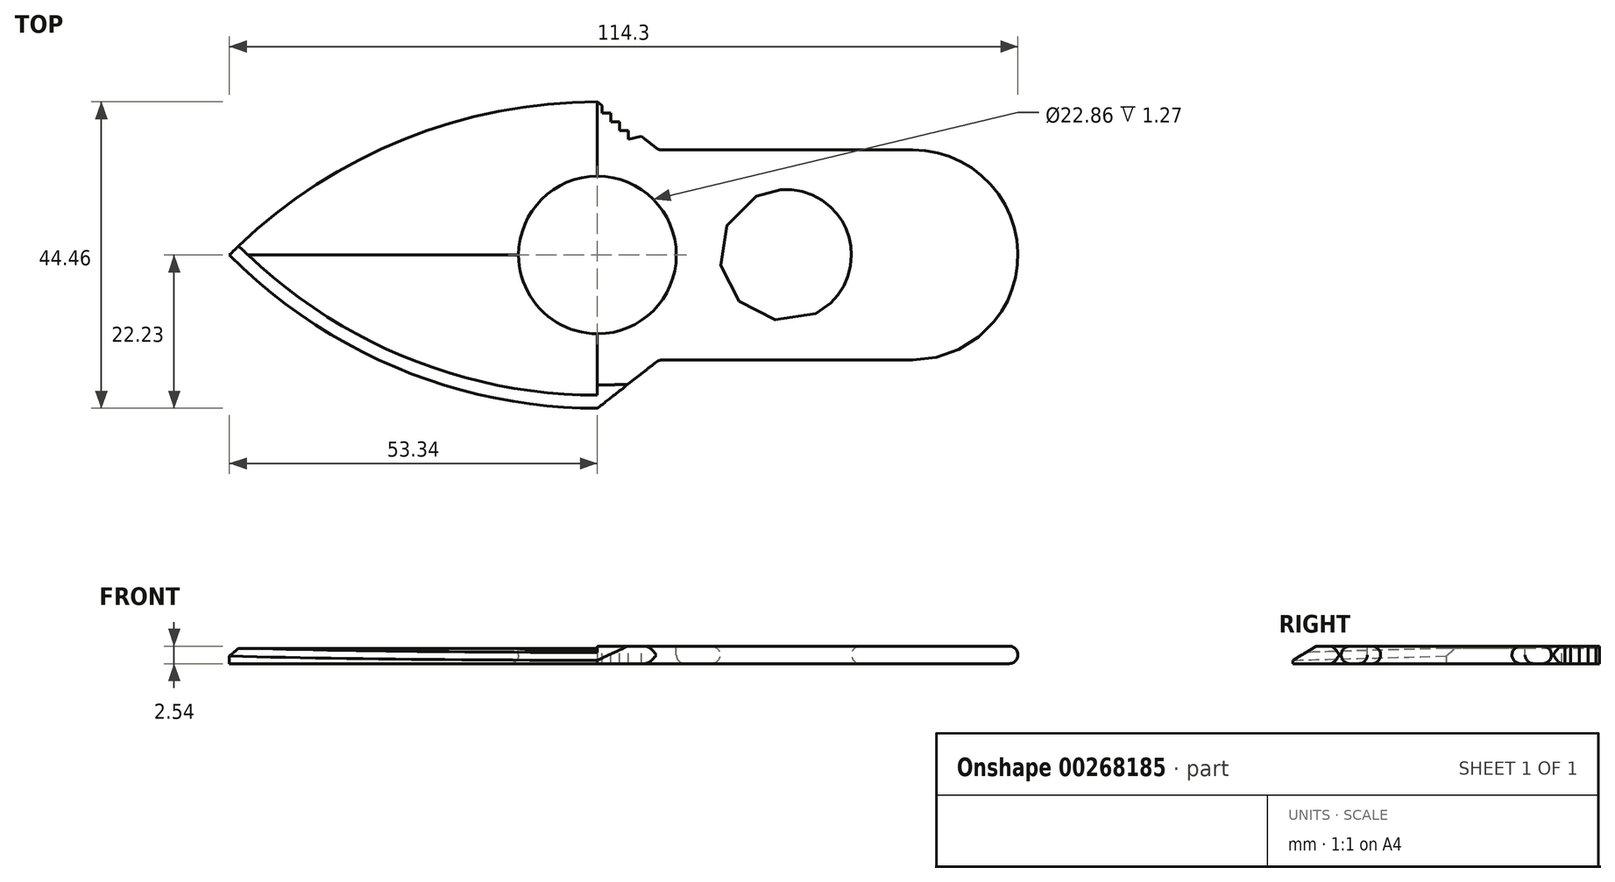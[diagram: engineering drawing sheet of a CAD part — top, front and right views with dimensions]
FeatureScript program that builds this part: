
annotation { "Feature Type Name" : "Feature", "Feature Type Description" : "" }
export const myFeature = defineFeature(function(context is Context, id is Id, definition is map)
    precondition{}
    {
        {
            var Q0;
            Q0=qCreatedBy(makeId("Top.planeOp"),FACE);
            var sketch = newSketch(context, id + "F0", { "sketchPlane" : qUnion([Q0])});
            skLineSegment(sketch, "E0", {"start": v(-57.15, 0) * mm, "end": v(57.15, 0) * mm});
            skArc(sketch, "E1", {"start": v(-3.81, 22.23) * mm, "mid": v(-32.7, 16.45) * mm, "end": v(-57.15, 0) * mm});
            skLineSegment(sketch, "E2", {"start": v(-3.8, 22.23) * mm, "end": v(-3.8, 0) * mm, "construction": true});
            skLineSegment(sketch, "E3", {"start": v(5.08, 15.24) * mm, "end": v(41.91, 15.24) * mm});
            skLineSegment(sketch, "E4", {"start": v(41.91, 15.24) * mm, "end": v(41.91, 0) * mm, "construction": true});
            skLineSegment(sketch, "E5", {"start": v(5.08, 15.24) * mm, "end": v(5.08, 0) * mm, "construction": true});
            skLineSegment(sketch, "E6", {"start": v(-3.81, 22.23) * mm, "end": v(5.08, 15.24) * mm});
            skLineSegment(sketch, "E7", {"start": v(-3.81, 22.23) * mm, "end": v(-57.15, 22.22) * mm, "construction": true});
            skArc(sketch, "E8", {"start": v(57.15, 0) * mm, "mid": v(52.69, 10.78) * mm, "end": v(41.91, 15.24) * mm});
            skLineSegment(sketch, "E9", {"start": v(57.15, 0) * mm, "end": v(57.15, 15.24) * mm, "construction": true});
            skSolve(sketch);
        }
        {
            var Q0;
            Q0 = qSketchRegion(id + "F0", true);
            extrude(context, id + "F1", {"entities" : qUnion([Q0]), "endBound" : BoundingType.SYMMETRIC, "depth" : 2.54 * mm});
        }
        {
            var Q0;
            Q0=makeQuery(id+"F1.opExtrude","SWEPT_BODY",BODY,{"disambiguationData":[OSD([sQuery(id+"F0.wireOp",EDGE,"E0"),sQuery(id+"F0.wireOp",EDGE,"E1"),sQuery(id+"F0.wireOp",EDGE,"E3"),sQuery(id+"F0.wireOp",EDGE,"E6"),sQuery(id+"F0.wireOp",EDGE,"E8")])]});
            var Q1;
            Q1=qCreatedBy(makeId("Front.planeOp"),FACE);
            mirror(context, id + "F2", {"operationType" : NewBodyOperationType.ADD, "entities" : qUnion([Q0]), "mirrorPlane" : qUnion([Q1])});
        }
        {
            var Q0;
            {var subQ0=makeQuery(id+"F1.opExtrude","CAP_FACE",FACE,{"disambiguationData":[OSD([sQuery(id+"F0.wireOp",EDGE,"E0"),sQuery(id+"F0.wireOp",EDGE,"E1"),sQuery(id+"F0.wireOp",EDGE,"E3"),sQuery(id+"F0.wireOp",EDGE,"E6"),sQuery(id+"F0.wireOp",EDGE,"E8")])],"isStart":false});Q0=makeQuery(id+"F2.boolean.opBoolean","MERGE",FACE,{"derivedFrom":[subQ0,makeQuery(id+"F2.opPattern","COPY",FACE,{"derivedFrom":subQ0,"instanceName":"1"})]});}
            var sketch = newSketch(context, id + "F3", { "sketchPlane" : qUnion([Q0])});
            skCircle(sketch, "E10", {"center": v(-3.81, 0) * mm, "radius": 11.43 * mm});
            skLineSegment(sketch, "E11", {"start": v(-3.81, 22.23) * mm, "end": v(-3.81, 6.18) * mm, "construction": true});
            skLineSegment(sketch, "E12", {"start": v(5.08, 15.24) * mm, "end": v(5.08, 6.18) * mm, "construction": true});
            skLineSegment(sketch, "E13", {"start": v(-3.81, 6.18) * mm, "end": v(5.08, 6.18) * mm, "construction": true});
            skCircle(sketch, "E14", {"center": v(23.5, 0) * mm, "radius": 9.53 * mm});
            skLineSegment(sketch, "E15", {"start": v(7.62, 0) * mm, "end": v(13.97, 0) * mm, "construction": true});
            skSolve(sketch);
        }
        {
            var Q0;
            Q0 = qSketchRegion(id + "F3", true);
            extrude(context, id + "F4", {"entities" : qUnion([Q0]), "operationType" : NewBodyOperationType.REMOVE, "endBound" : BoundingType.THROUGH_ALL, "oppositeDirection" : true, "depth" : 25.4 * mm});
        }
        {
            var Q0;
            {var subQ0=makeQuery(id+"F1.opExtrude","CAP_FACE",FACE,{"disambiguationData":[OSD([sQuery(id+"F0.wireOp",EDGE,"E0"),sQuery(id+"F0.wireOp",EDGE,"E1"),sQuery(id+"F0.wireOp",EDGE,"E3"),sQuery(id+"F0.wireOp",EDGE,"E6"),sQuery(id+"F0.wireOp",EDGE,"E8")])],"isStart":false});Q0=makeQuery(id+"F2.boolean.opBoolean","MERGE",FACE,{"derivedFrom":[subQ0,makeQuery(id+"F2.opPattern","COPY",FACE,{"derivedFrom":subQ0,"instanceName":"1"})]});}
            var sketch = newSketch(context, id + "F5", { "sketchPlane" : qUnion([Q0])});
            skLineSegment(sketch, "E16", {"start": v(-3.81, 22.23) * mm, "end": v(-3.81, -22.23) * mm});
            skArc(sketch, "E17", {"start": v(-57.15, 0) * mm, "mid": v(-32.7, -16.45) * mm, "end": v(-3.8, -22.22) * mm});
            skArc(sketch, "E18", {"start": v(-3.81, 22.23) * mm, "mid": v(-32.7, 16.45) * mm, "end": v(-57.15, 0) * mm});
            skSolve(sketch);
        }
        {
            var Q0;
            Q0 = qSketchRegion(id + "F5", true);
            extrude(context, id + "F6", {"entities" : qUnion([Q0]), "operationType" : NewBodyOperationType.REMOVE, "oppositeDirection" : true, "depth" : 0.32 * mm});
        }
        {
            var Q0;
            {var subQ1=sQuery(id+"F0.wireOp",EDGE,"E1");var subQ3=sQuery(id+"F5.wireOp",EDGE,"E16");Q0=makeQuery(id+"F6.boolean.opBoolean","COPY",FACE,{"disambiguationData":[TD([makeQuery(id+"F2.opPattern","COPY",FACE,{"derivedFrom":makeQuery(id+"F1.opExtrude","SWEPT_FACE",FACE,{"disambiguationData":[OSD([subQ1])]}),"instanceName":"1"})])],"derivedFrom":makeQuery(id+"F6.opExtrude","SWEPT_FACE",FACE,{"disambiguationData":[OSD([subQ3])]})});}
            cPlane(context, id + "F7", {"entities" : qUnion([Q0]), "cplaneType" : CPlaneType.OFFSET, "offset" : 0 * mm, "width" : 152.4 * mm, "height" : 152.4 * mm});
        }
        {
            var Q0;
            Q0=qCreatedBy(id+"F7.planeOp",FACE);
            var sketch = newSketch(context, id + "F8", { "sketchPlane" : qUnion([Q0])});
            skLineSegment(sketch, "E19", {"start": v(0, 0.95) * mm, "end": v(22.23, 0.32) * mm});
            skLineSegment(sketch, "E20", {"start": v(22.23, 0.95) * mm, "end": v(0, 0.95) * mm});
            skLineSegment(sketch, "E21", {"start": v(22.23, 0.95) * mm, "end": v(22.23, 0.32) * mm});
            skSolve(sketch);
        }
        {
            var Q0;
            Q0 = qSketchRegion(id + "F8", true);
            extrude(context, id + "F9", {"entities" : qUnion([Q0]), "operationType" : NewBodyOperationType.REMOVE, "endBound" : BoundingType.THROUGH_ALL, "depth" : 25.4 * mm});
        }
        {
            var Q0;
            Q0=makeQuery(id+"F1.opExtrude","SWEPT_FACE",FACE,{"disambiguationData":[OSD([sQuery(id+"F0.wireOp",EDGE,"E3")])]});
            var Q1;
            {var subQ0=makeQuery(id+"F1.opExtrude","SWEPT_FACE",FACE,{"disambiguationData":[OSD([sQuery(id+"F0.wireOp",EDGE,"E8")])]});Q1=makeQuery(id+"F2.boolean.opBoolean","MERGE",FACE,{"derivedFrom":[subQ0,makeQuery(id+"F2.opPattern","COPY",FACE,{"derivedFrom":subQ0,"instanceName":"1"})]});}
            var Q2;
            Q2=makeQuery(id+"F2.opPattern","COPY",FACE,{"derivedFrom":makeQuery(id+"F1.opExtrude","SWEPT_FACE",FACE,{"disambiguationData":[OSD([sQuery(id+"F0.wireOp",EDGE,"E3")])]}),"instanceName":"1"});
            fillet(context, id + "F10", {"entities" : qUnion([Q0, Q1, Q2]), "radius" : 1.27 * mm, "allowEdgeOverflow" : false});
        }
        {
            var Q0;
            Q0=makeQuery(id+"F9.boolean.opBoolean","INTERSECT",EDGE,{"derivedFrom":[makeQuery(id+"F2.opPattern","COPY",FACE,{"derivedFrom":makeQuery(id+"F1.opExtrude","SWEPT_FACE",FACE,{"disambiguationData":[OSD([sQuery(id+"F0.wireOp",EDGE,"E1")])]}),"instanceName":"1"}),makeQuery(id+"F9.opExtrude","SWEPT_FACE",FACE,{"disambiguationData":[OSD([sQuery(id+"F8.wireOp",EDGE,"E19")])]})]});
            var Q1;
            Q1=makeQuery(id+"F8juky5xSXw5ZZ9_1.1.F9.boolean.opBoolean","INTERSECT",EDGE,{"derivedFrom":[makeQuery(id+"F2.opPattern","COPY",FACE,{"derivedFrom":makeQuery(id+"F1.opExtrude","SWEPT_FACE",FACE,{"disambiguationData":[OSD([sQuery(id+"F0.wireOp",EDGE,"E1")])]}),"instanceName":"1"}),makeQuery(id+"F8juky5xSXw5ZZ9_1.1.F9.opExtrude","SWEPT_FACE",FACE,{"disambiguationData":[OSD([sQuery(id+"F8.wireOp",EDGE,"E19")])]})]});
            chamfer(context, id + "F11", {"entities" : qUnion([Q0, Q1]), "chamferType" : ChamferType.OFFSET_ANGLE, "width" : 1.9 * mm, "oppositeDirection" : false, "angle" : 30 * degree, "tangentPropagation" : true});
        }
        {
            var Q0;
            {var subQ0=makeQuery(id+"F1.opExtrude","CAP_FACE",FACE,{"disambiguationData":[OSD([sQuery(id+"F0.wireOp",EDGE,"E0"),sQuery(id+"F0.wireOp",EDGE,"E1"),sQuery(id+"F0.wireOp",EDGE,"E3"),sQuery(id+"F0.wireOp",EDGE,"E6"),sQuery(id+"F0.wireOp",EDGE,"E8")])],"isStart":false});Q0=makeQuery(id+"F2.boolean.opBoolean","MERGE",FACE,{"derivedFrom":[subQ0,makeQuery(id+"F2.opPattern","COPY",FACE,{"derivedFrom":subQ0,"instanceName":"1"})]});}
            var sketch = newSketch(context, id + "F12", { "sketchPlane" : qUnion([Q0])});
            skLineSegment(sketch, "E22", {"start": v(0.67, 16.76) * mm, "end": v(0.67, 18.03) * mm});
            skLineSegment(sketch, "E23", {"start": v(-0.4, 19.55) * mm, "end": v(-0.6, 19.3) * mm, "construction": true});
            skLineSegment(sketch, "E24", {"start": v(0.67, 18.03) * mm, "end": v(-0.6, 18.03) * mm});
            skLineSegment(sketch, "E25", {"start": v(-0.6, 18.03) * mm, "end": v(-0.6, 19.3) * mm});
            skLineSegment(sketch, "E26", {"start": v(-0.6, 19.3) * mm, "end": v(-1.87, 19.3) * mm});
            skLineSegment(sketch, "E27", {"start": v(-1.87, 19.3) * mm, "end": v(-1.87, 20.57) * mm});
            skLineSegment(sketch, "E28", {"start": v(-1.87, 20.57) * mm, "end": v(-3.14, 20.57) * mm});
            skLineSegment(sketch, "E29", {"start": v(-3.14, 20.57) * mm, "end": v(-3.14, 21.7) * mm});
            skLineSegment(sketch, "E30", {"start": v(0.67, 16.76) * mm, "end": v(2.58, 17.2) * mm});
            skLineSegment(sketch, "E31", {"start": v(-3.14, 21.7) * mm, "end": v(2.58, 17.2) * mm});
            skSolve(sketch);
        }
        {
            var Q0;
            Q0 = qSketchRegion(id + "F12", true);
            extrude(context, id + "F13", {"entities" : qUnion([Q0]), "operationType" : NewBodyOperationType.REMOVE, "endBound" : BoundingType.THROUGH_ALL, "oppositeDirection" : true, "depth" : 25.4 * mm, "hasSecondDirection" : true, "secondDirectionBound" : SecondDirectionBoundingType.THROUGH_ALL, "secondDirectionOppositeDirection" : false, "secondDirectionDepth" : 25.4 * mm});
        }
        {
            var Q0;
            Q0=makeQuery(id+"F4.boolean.opBoolean","COPY",FACE,{"derivedFrom":makeQuery(id+"F4.opExtrude","SWEPT_FACE",FACE,{"disambiguationData":[OSD([sQuery(id+"F3.wireOp",EDGE,"E14")])]})});
            fillet(context, id + "F14", {"entities" : qUnion([Q0]), "radius" : 1.27 * mm, "tangentPropagation" : true, "allowEdgeOverflow" : false});
        }
        {
            var Q0;
            Q0=makeQuery(id+"F4.boolean.opBoolean","COPY",EDGE,{"derivedFrom":makeQuery(id+"F4.opExtrude","CAP_EDGE",EDGE,{"disambiguationData":[OSD([sQuery(id+"F3.wireOp",EDGE,"E10")])],"isStart":true})});
            var Q1;
            {var subQ0=makeQuery(id+"F1.opExtrude","CAP_FACE",FACE,{"disambiguationData":[OSD([sQuery(id+"F0.wireOp",EDGE,"E0"),sQuery(id+"F0.wireOp",EDGE,"E1"),sQuery(id+"F0.wireOp",EDGE,"E3"),sQuery(id+"F0.wireOp",EDGE,"E6"),sQuery(id+"F0.wireOp",EDGE,"E8")])],"isStart":true});Q1=makeQuery(id+"F4.boolean.opBoolean","INTERSECT",EDGE,{"derivedFrom":[makeQuery(id+"F2.boolean.opBoolean","MERGE",FACE,{"derivedFrom":[subQ0,makeQuery(id+"F2.opPattern","COPY",FACE,{"derivedFrom":subQ0,"instanceName":"1"})]}),makeQuery(id+"F4.opExtrude","SWEPT_FACE",FACE,{"disambiguationData":[OSD([sQuery(id+"F3.wireOp",EDGE,"E10")])]})]});}
            fillet(context, id + "F15", {"entities" : qUnion([Q0, Q1]), "radius" : 1.27 * mm, "tangentPropagation" : true, "allowEdgeOverflow" : false});
        }
    });
